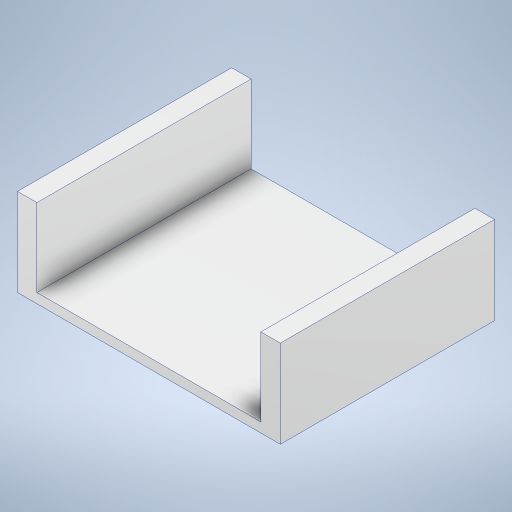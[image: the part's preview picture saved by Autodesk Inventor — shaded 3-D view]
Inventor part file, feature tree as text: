
AUTODESK INVENTOR PART (.ipt)
format: ipt  version: 2024 (Build 280153000, 153)  size: 232,448 bytes
history: native  units: mm
features: extrude x2, sketch x2
ambient origin geometry x8: Origin, YZ Plane, XZ Plane, XY Plane, X Axis, Y Axis, Z Axis, Center Point
bodies: Solid1 (feature_tree)
feature tree (4):
  extrude  "Extrusion1"  Depth=230.0mm
  extrude  "Extrusion5"  Depth=90.0mm
  sketch  "Sketch1"  dims[d0=220.0mm d1=230.0mm]
  sketch  "Sketch5"  dims[d2=10.0mm d3=0.0mm d22=90.0mm d23=20.0mm d24=20.0mm d25=10.0mm d26=0.0mm]
